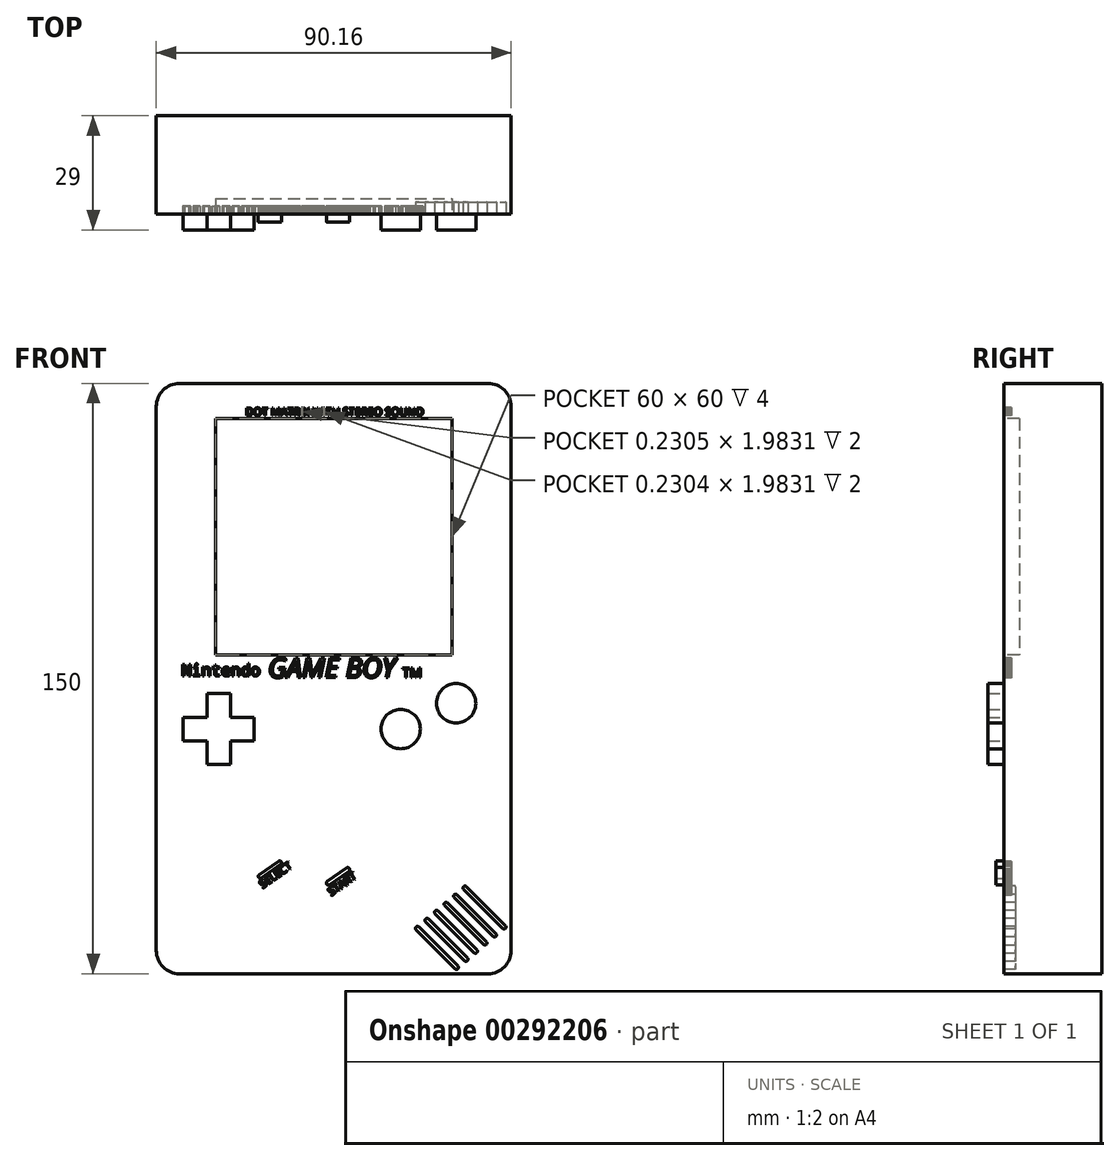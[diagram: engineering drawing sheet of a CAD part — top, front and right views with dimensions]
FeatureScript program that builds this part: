
annotation { "Feature Type Name" : "Feature", "Feature Type Description" : "" }
export const myFeature = defineFeature(function(context is Context, id is Id, definition is map)
    precondition{}
    {
        {
            var Q0;
            Q0=qCreatedBy(makeId("Front.planeOp"),FACE);
            var sketch = newSketch(context, id + "F0", { "sketchPlane" : qUnion([Q0])});
            skLineSegment(sketch, "E0", {"start": v(-45.08, 81.93) * mm, "end": v(-45.08, -35.2) * mm});
            skLineSegment(sketch, "E1", {"start": v(-45.08, -35.2) * mm, "end": v(-45.08, -56.28) * mm});
            skLineSegment(sketch, "E2", {"start": v(-39.18, 87.83) * mm, "end": v(0, 87.83) * mm});
            skLineSegment(sketch, "E3", {"start": v(0, 87.83) * mm, "end": v(0, -62.17) * mm, "construction": true});
            skLineSegment(sketch, "E4", {"start": v(0, -62.17) * mm, "end": v(-39.18, -62.17) * mm});
            skLineSegment(sketch, "E5.MirrorCS", {"start": v(45.08, -35.2) * mm, "end": v(45.08, -56.27) * mm});
            skLineSegment(sketch, "E6.MirrorCS", {"start": v(39.18, 87.83) * mm, "end": v(0, 87.83) * mm});
            skLineSegment(sketch, "E7.MirrorCS", {"start": v(0, -62.17) * mm, "end": v(39.18, -62.17) * mm});
            skLineSegment(sketch, "E8.MirrorCS", {"start": v(45.08, 81.93) * mm, "end": v(45.08, -35.2) * mm});
            skPoint(sketch, "E9.visualSharp", {"position": v(-45.08, 87.83) * mm});
            skArc(sketch, "E9.filletArc", {"start": v(-39.18, 87.83) * mm, "mid": v(-43.35, 86.1) * mm, "end": v(-45.08, 81.93) * mm});
            skPoint(sketch, "E10.visualSharp", {"position": v(-45.08, -62.17) * mm});
            skArc(sketch, "E10.filletArc", {"start": v(-45.08, -56.28) * mm, "mid": v(-43.35, -60.44) * mm, "end": v(-39.18, -62.17) * mm});
            skPoint(sketch, "E11.visualSharp", {"position": v(45.08, 87.83) * mm});
            skArc(sketch, "E11.filletArc", {"start": v(45.08, 81.93) * mm, "mid": v(43.35, 86.1) * mm, "end": v(39.18, 87.83) * mm});
            skPoint(sketch, "E12.visualSharp", {"position": v(45.08, -62.17) * mm});
            skArc(sketch, "E12.filletArc", {"start": v(39.18, -62.17) * mm, "mid": v(43.35, -60.44) * mm, "end": v(45.08, -56.27) * mm});
            skSolve(sketch);
        }
        {
            var Q0;
            Q0=makeQuery(id+"F0.imprint","IMPRINT",FACE,{"disambiguationData":[TD([[makeQuery(id+"F0.imprint","IMPRINT",EDGE,{"derivedFrom":sQuery(id+"F0.wireOp",EDGE,"E0")}),1.0]])]});
            extrude(context, id + "F1", {"entities" : qUnion([Q0]), "depth" : 25 * mm});
        }
        {
            var Q0;
            Q0=makeQuery(id+"F1.opExtrude","CAP_FACE",FACE,{"disambiguationData":[OSD([sQuery(id+"F0.wireOp",EDGE,"E0"),sQuery(id+"F0.wireOp",EDGE,"E1"),sQuery(id+"F0.wireOp",EDGE,"E2"),sQuery(id+"F0.wireOp",EDGE,"E4"),sQuery(id+"F0.wireOp",EDGE,"E5.MirrorCS"),sQuery(id+"F0.wireOp",EDGE,"E6.MirrorCS"),sQuery(id+"F0.wireOp",EDGE,"E7.MirrorCS"),sQuery(id+"F0.wireOp",EDGE,"E8.MirrorCS"),sQuery(id+"F0.wireOp",EDGE,"E9.filletArc"),sQuery(id+"F0.wireOp",EDGE,"E10.filletArc"),sQuery(id+"F0.wireOp",EDGE,"E11.filletArc"),sQuery(id+"F0.wireOp",EDGE,"E12.filletArc")])],"isStart":false});
            var sketch = newSketch(context, id + "F2", { "sketchPlane" : qUnion([Q0])});
            skPoint(sketch, "E13.centerSnap0", {"position": v(45.08, 12.83) * mm});
            skCircle(sketch, "E14", {"center": v(31.09, 6.56) * mm, "radius": 5 * mm});
            skCircle(sketch, "E15", {"center": v(17, 0) * mm, "radius": 5 * mm});
            skLineSegment(sketch, "E16", {"start": v(-29.21, 14.04) * mm, "end": v(-29.21, -22.61) * mm, "construction": true});
            skLineSegment(sketch, "E17", {"start": v(-38.21, 0) * mm, "end": v(-38.21, 3) * mm});
            skLineSegment(sketch, "E18", {"start": v(-38.21, 3) * mm, "end": v(-32.21, 3) * mm});
            skLineSegment(sketch, "E19", {"start": v(-32.21, 3) * mm, "end": v(-32.21, 9) * mm});
            skLineSegment(sketch, "E20", {"start": v(-32.21, 9) * mm, "end": v(-29.21, 9) * mm});
            skLineSegment(sketch, "E21.MirrorCS", {"start": v(-20.21, 0) * mm, "end": v(-20.21, 3) * mm});
            skLineSegment(sketch, "E22.MirrorCS", {"start": v(-20.21, 3) * mm, "end": v(-26.21, 3) * mm});
            skLineSegment(sketch, "E23.MirrorCS", {"start": v(-26.21, 3) * mm, "end": v(-26.21, 9) * mm});
            skLineSegment(sketch, "E24.MirrorCS", {"start": v(-26.21, 9) * mm, "end": v(-29.21, 9) * mm});
            skLineSegment(sketch, "E25", {"start": v(-47.45, 0) * mm, "end": v(-14.16, 0) * mm, "construction": true});
            skLineSegment(sketch, "E26.MirrorCS", {"start": v(-38.21, 0) * mm, "end": v(-38.21, -3) * mm});
            skLineSegment(sketch, "E27.MirrorCS", {"start": v(-38.21, -3) * mm, "end": v(-32.21, -3) * mm});
            skLineSegment(sketch, "E28.MirrorCS", {"start": v(-32.21, -3) * mm, "end": v(-32.21, -9) * mm});
            skLineSegment(sketch, "E29.MirrorCS", {"start": v(-32.21, -9) * mm, "end": v(-29.21, -9) * mm});
            skLineSegment(sketch, "E30.MirrorCS", {"start": v(-26.21, -9) * mm, "end": v(-29.21, -9) * mm});
            skLineSegment(sketch, "E31.MirrorCS", {"start": v(-26.21, -3) * mm, "end": v(-26.21, -9) * mm});
            skLineSegment(sketch, "E32.MirrorCS", {"start": v(-20.21, -3) * mm, "end": v(-26.21, -3) * mm});
            skLineSegment(sketch, "E33.MirrorCS", {"start": v(-20.21, 0) * mm, "end": v(-20.21, -3) * mm});
            skLineSegment(sketch, "E34", {"start": v(0, 79.93) * mm, "end": v(0, 21.08) * mm, "construction": true});
            skLineSegment(sketch, "E35", {"start": v(0, 79.93) * mm, "end": v(-30, 79.93) * mm});
            skLineSegment(sketch, "E36", {"start": v(-30, 79.93) * mm, "end": v(-30, 19.93) * mm});
            skLineSegment(sketch, "E37", {"start": v(-30, 19.93) * mm, "end": v(0, 19.93) * mm});
            skLineSegment(sketch, "E38.MirrorCS", {"start": v(0, 79.93) * mm, "end": v(30, 79.93) * mm});
            skLineSegment(sketch, "E39.MirrorCS", {"start": v(30, 79.93) * mm, "end": v(30, 19.93) * mm});
            skLineSegment(sketch, "E40.MirrorCS", {"start": v(30, 19.93) * mm, "end": v(0, 19.93) * mm});
            skSolve(sketch);
        }
        {
            var Q0;
            Q0=makeQuery(id+"F2.imprint","IMPRINT",FACE,{"disambiguationData":[TD([[makeQuery(id+"F2.imprint","IMPRINT",EDGE,{"derivedFrom":sQuery(id+"F2.wireOp",EDGE,"E14")}),1.0]])]});
            var Q1;
            Q1=makeQuery(id+"F2.imprint","IMPRINT",FACE,{"disambiguationData":[TD([[makeQuery(id+"F2.imprint","IMPRINT",EDGE,{"derivedFrom":sQuery(id+"F2.wireOp",EDGE,"E15")}),1.0]])]});
            var Q2;
            Q2=makeQuery(id+"F2.imprint","IMPRINT",FACE,{"disambiguationData":[TD([[makeQuery(id+"F2.imprint","IMPRINT",EDGE,{"derivedFrom":sQuery(id+"F2.wireOp",EDGE,"E17")}),-1.0]])]});
            extrude(context, id + "F3", {"entities" : qUnion([Q0, Q1, Q2]), "operationType" : NewBodyOperationType.ADD, "depth" : 4 * mm});
        }
        {
            var Q0;
            Q0=makeQuery(id+"F1.opExtrude","CAP_FACE",FACE,{"disambiguationData":[OSD([sQuery(id+"F0.wireOp",EDGE,"E0"),sQuery(id+"F0.wireOp",EDGE,"E1"),sQuery(id+"F0.wireOp",EDGE,"E2"),sQuery(id+"F0.wireOp",EDGE,"E4"),sQuery(id+"F0.wireOp",EDGE,"E5.MirrorCS"),sQuery(id+"F0.wireOp",EDGE,"E6.MirrorCS"),sQuery(id+"F0.wireOp",EDGE,"E7.MirrorCS"),sQuery(id+"F0.wireOp",EDGE,"E8.MirrorCS"),sQuery(id+"F0.wireOp",EDGE,"E9.filletArc"),sQuery(id+"F0.wireOp",EDGE,"E10.filletArc"),sQuery(id+"F0.wireOp",EDGE,"E11.filletArc"),sQuery(id+"F0.wireOp",EDGE,"E12.filletArc")])],"isStart":false});
            var sketch = newSketch(context, id + "F4", { "sketchPlane" : qUnion([Q0])});
            skSolve(sketch);
        }
        {
            var Q0;
            Q0=makeQuery(id+"F4.imprint","IMPRINT",FACE,{"disambiguationData":[TD([[makeQuery(id+"F4.imprint","IMPRINT",EDGE,{"derivedFrom":makeQuery(id+"F1.opExtrude","CAP_EDGE",EDGE,{"disambiguationData":[OSD([sQuery(id+"F0.wireOp",EDGE,"E9.filletArc")])],"isStart":false})}),1.0]])]});
            var sketch = newSketch(context, id + "F5", { "sketchPlane" : qUnion([Q0])});
            skLineSegment(sketch, "E41.bottom", {"start": v(-30, 78.85) * mm, "end": v(30, 78.85) * mm});
            skLineSegment(sketch, "E41.top", {"start": v(-30, 18.85) * mm, "end": v(30, 18.85) * mm});
            skLineSegment(sketch, "E41.left", {"start": v(-30, 78.85) * mm, "end": v(-30, 18.85) * mm});
            skLineSegment(sketch, "E41.right", {"start": v(30, 78.85) * mm, "end": v(30, 18.85) * mm});
            skLineSegment(sketch, "E42", {"start": v(0, 0) * mm, "end": v(0, 81.4) * mm, "construction": true});
            skLineSegment(sketch, "E43", {"start": v(0, 81.4) * mm, "end": v(0, 43.76) * mm, "construction": true});
            skSolve(sketch);
        }
        {
            var Q0;
            Q0 = qSketchRegion(id + "F5", true);
            var Q1;
            Q1=makeQuery(id+"F5.imprint","IMPRINT",FACE,{"disambiguationData":[TD([[makeQuery(id+"F5.imprint","IMPRINT",EDGE,{"derivedFrom":sQuery(id+"F5.wireOp",EDGE,"E41.bottom")}),-1.0]])]});
            extrude(context, id + "F6", {"entities" : qUnion([Q0, Q1]), "operationType" : NewBodyOperationType.REMOVE, "oppositeDirection" : true, "depth" : 4 * mm});
        }
        {
            var Q0;
            Q0=makeQuery(id+"F4.imprint","IMPRINT",FACE,{"disambiguationData":[TD([[makeQuery(id+"F4.imprint","IMPRINT",EDGE,{"derivedFrom":makeQuery(id+"F1.opExtrude","CAP_EDGE",EDGE,{"disambiguationData":[OSD([sQuery(id+"F0.wireOp",EDGE,"E9.filletArc")])],"isStart":false})}),1.0]])]});
            var sketch = newSketch(context, id + "F7", { "sketchPlane" : qUnion([Q0])});
            skLineSegment(sketch, "E44", {"start": v(33.02, -40.75) * mm, "end": v(42.92, -50.65) * mm});
            skLineSegment(sketch, "E45", {"start": v(33.02, -40.04) * mm, "end": v(33.02, -40.04) * mm});
            skLineSegment(sketch, "E46", {"start": v(33.72, -40.04) * mm, "end": v(43.63, -49.94) * mm});
            skLineSegment(sketch, "E47", {"start": v(43.62, -50.65) * mm, "end": v(43.62, -50.65) * mm});
            skPoint(sketch, "E48.visualSharp", {"position": v(32.66, -40.4) * mm});
            skArc(sketch, "E48.filletArc", {"start": v(33.02, -40.04) * mm, "mid": v(32.87, -40.4) * mm, "end": v(33.02, -40.75) * mm});
            skPoint(sketch, "E49.visualSharp", {"position": v(33.37, -39.69) * mm});
            skArc(sketch, "E49.filletArc", {"start": v(33.72, -40.04) * mm, "mid": v(33.37, -39.9) * mm, "end": v(33.02, -40.04) * mm});
            skPoint(sketch, "E50.visualSharp", {"position": v(43.27, -51) * mm});
            skArc(sketch, "E50.filletArc", {"start": v(42.92, -50.65) * mm, "mid": v(43.27, -50.8) * mm, "end": v(43.62, -50.65) * mm});
            skPoint(sketch, "E51.visualSharp", {"position": v(43.98, -50.3) * mm});
            skArc(sketch, "E51.filletArc", {"start": v(43.62, -50.65) * mm, "mid": v(43.77, -50.3) * mm, "end": v(43.63, -49.94) * mm});
            skLineSegment(sketch, "E52", {"start": v(26.9, -56.2) * mm, "end": v(43.42, -39.67) * mm, "construction": true});
            skLineSegment(sketch, "E53.1.0.0", {"start": v(30.6, -42.8) * mm, "end": v(40.5, -52.7) * mm});
            skLineSegment(sketch, "E53.1.0.1", {"start": v(31.3, -42.1) * mm, "end": v(41.2, -52) * mm});
            skArc(sketch, "E53.1.0.2", {"start": v(30.6, -42.1) * mm, "mid": v(30.45, -42.45) * mm, "end": v(30.6, -42.8) * mm});
            skArc(sketch, "E53.1.0.3", {"start": v(31.3, -42.1) * mm, "mid": v(30.95, -41.95) * mm, "end": v(30.6, -42.1) * mm});
            skArc(sketch, "E53.1.0.4", {"start": v(40.5, -52.7) * mm, "mid": v(40.85, -52.85) * mm, "end": v(41.2, -52.7) * mm});
            skArc(sketch, "E53.1.0.5", {"start": v(41.2, -52.7) * mm, "mid": v(41.35, -52.35) * mm, "end": v(41.2, -52) * mm});
            skLineSegment(sketch, "E53.2.0.0", {"start": v(28.18, -44.85) * mm, "end": v(38.08, -54.75) * mm});
            skLineSegment(sketch, "E53.2.0.1", {"start": v(28.89, -44.14) * mm, "end": v(38.79, -54.04) * mm});
            skArc(sketch, "E53.2.0.2", {"start": v(28.18, -44.14) * mm, "mid": v(28.03, -44.5) * mm, "end": v(28.18, -44.85) * mm});
            skArc(sketch, "E53.2.0.3", {"start": v(28.89, -44.14) * mm, "mid": v(28.53, -44) * mm, "end": v(28.18, -44.14) * mm});
            skArc(sketch, "E53.2.0.4", {"start": v(38.08, -54.75) * mm, "mid": v(38.43, -54.9) * mm, "end": v(38.79, -54.75) * mm});
            skArc(sketch, "E53.2.0.5", {"start": v(38.79, -54.75) * mm, "mid": v(38.93, -54.4) * mm, "end": v(38.79, -54.04) * mm});
            skLineSegment(sketch, "E53.3.0.0", {"start": v(25.76, -46.9) * mm, "end": v(35.66, -56.8) * mm});
            skLineSegment(sketch, "E53.3.0.1", {"start": v(26.47, -46.2) * mm, "end": v(36.37, -56.1) * mm});
            skArc(sketch, "E53.3.0.2", {"start": v(25.76, -46.2) * mm, "mid": v(25.62, -46.55) * mm, "end": v(25.76, -46.9) * mm});
            skArc(sketch, "E53.3.0.3", {"start": v(26.47, -46.2) * mm, "mid": v(26.12, -46.05) * mm, "end": v(25.76, -46.2) * mm});
            skArc(sketch, "E53.3.0.4", {"start": v(35.66, -56.8) * mm, "mid": v(36.02, -56.95) * mm, "end": v(36.37, -56.8) * mm});
            skArc(sketch, "E53.3.0.5", {"start": v(36.37, -56.8) * mm, "mid": v(36.52, -56.45) * mm, "end": v(36.37, -56.1) * mm});
            skLineSegment(sketch, "E53.4.0.0", {"start": v(23.34, -48.95) * mm, "end": v(33.24, -58.85) * mm});
            skLineSegment(sketch, "E53.4.0.1", {"start": v(24.05, -48.24) * mm, "end": v(33.95, -58.15) * mm});
            skArc(sketch, "E53.4.0.2", {"start": v(23.34, -48.24) * mm, "mid": v(23.2, -48.6) * mm, "end": v(23.34, -48.95) * mm});
            skArc(sketch, "E53.4.0.3", {"start": v(24.05, -48.24) * mm, "mid": v(23.7, -48.1) * mm, "end": v(23.34, -48.24) * mm});
            skArc(sketch, "E53.4.0.4", {"start": v(33.24, -58.85) * mm, "mid": v(33.6, -59) * mm, "end": v(33.95, -58.85) * mm});
            skArc(sketch, "E53.4.0.5", {"start": v(33.95, -58.85) * mm, "mid": v(34.1, -58.5) * mm, "end": v(33.95, -58.15) * mm});
            skLineSegment(sketch, "E53.5.0.0", {"start": v(20.92, -51) * mm, "end": v(30.83, -60.9) * mm});
            skLineSegment(sketch, "E53.5.0.1", {"start": v(21.63, -50.3) * mm, "end": v(31.53, -60.2) * mm});
            skArc(sketch, "E53.5.0.2", {"start": v(20.92, -50.3) * mm, "mid": v(20.78, -50.65) * mm, "end": v(20.92, -51) * mm});
            skArc(sketch, "E53.5.0.3", {"start": v(21.63, -50.3) * mm, "mid": v(21.28, -50.15) * mm, "end": v(20.92, -50.3) * mm});
            skArc(sketch, "E53.5.0.4", {"start": v(30.83, -60.9) * mm, "mid": v(31.18, -61.05) * mm, "end": v(31.53, -60.9) * mm});
            skArc(sketch, "E53.5.0.5", {"start": v(31.53, -60.9) * mm, "mid": v(31.68, -60.55) * mm, "end": v(31.53, -60.2) * mm});
            skLineSegment(sketch, "E53.direction1", {"start": v(42.92, -50.65) * mm, "end": v(40.5, -52.7) * mm, "construction": true});
            skSolve(sketch);
        }
        {
            var Q0;
            Q0 = qSketchRegion(id + "F7", true);
            extrude(context, id + "F8", {"entities" : qUnion([Q0]), "operationType" : NewBodyOperationType.REMOVE, "oppositeDirection" : true, "depth" : 3 * mm});
        }
        {
            var Q0;
            Q0=makeQuery(id+"F4.imprint","IMPRINT",FACE,{"disambiguationData":[TD([[makeQuery(id+"F4.imprint","IMPRINT",EDGE,{"derivedFrom":makeQuery(id+"F1.opExtrude","CAP_EDGE",EDGE,{"disambiguationData":[OSD([sQuery(id+"F0.wireOp",EDGE,"E9.filletArc")])],"isStart":false})}),1.0]])]});
            var sketch = newSketch(context, id + "F9", { "sketchPlane" : qUnion([Q0])});
            skLineSegment(sketch, "E54", {"start": v(-14.03, -33.56) * mm, "end": v(-18.95, -37) * mm});
            skLineSegment(sketch, "E55", {"start": v(-19.07, -37.7) * mm, "end": v(-19.07, -37.7) * mm});
            skLineSegment(sketch, "E56", {"start": v(-18.38, -37.83) * mm, "end": v(-13.46, -34.38) * mm});
            skLineSegment(sketch, "E57", {"start": v(-13.33, -33.7) * mm, "end": v(-13.33, -33.7) * mm});
            skPoint(sketch, "E58.visualSharp", {"position": v(-18.79, -38.11) * mm});
            skArc(sketch, "E58.filletArc", {"start": v(-19.07, -37.7) * mm, "mid": v(-18.75, -37.9) * mm, "end": v(-18.38, -37.83) * mm});
            skPoint(sketch, "E59.visualSharp", {"position": v(-19.36, -37.3) * mm});
            skArc(sketch, "E59.filletArc", {"start": v(-18.95, -37) * mm, "mid": v(-19.16, -37.33) * mm, "end": v(-19.07, -37.7) * mm});
            skPoint(sketch, "E60.visualSharp", {"position": v(-13.06, -34.1) * mm});
            skArc(sketch, "E60.filletArc", {"start": v(-13.46, -34.38) * mm, "mid": v(-13.25, -34.07) * mm, "end": v(-13.33, -33.7) * mm});
            skPoint(sketch, "E61.visualSharp", {"position": v(-13.6, -33.27) * mm});
            skArc(sketch, "E61.filletArc", {"start": v(-13.33, -33.7) * mm, "mid": v(-13.65, -33.48) * mm, "end": v(-14.03, -33.56) * mm});
            skPoint(sketch, "E62.1.0.0", {"position": v(4.22, -35.83) * mm});
            skLineSegment(sketch, "E62.1.0.1", {"start": v(3.25, -35.28) * mm, "end": v(-1.66, -38.73) * mm});
            skPoint(sketch, "E62.1.0.2", {"position": v(-1.5, -39.83) * mm});
            skPoint(sketch, "E62.1.0.3", {"position": v(-2.07, -39.01) * mm});
            skLineSegment(sketch, "E62.1.0.4", {"start": v(-1.1, -39.55) * mm, "end": v(3.83, -36.1) * mm});
            skPoint(sketch, "E62.1.0.5", {"position": v(3.68, -34.99) * mm});
            skArc(sketch, "E62.1.0.6", {"start": v(3.83, -36.1) * mm, "mid": v(4.03, -35.79) * mm, "end": v(3.96, -35.42) * mm});
            skArc(sketch, "E62.1.0.7", {"start": v(-1.66, -38.73) * mm, "mid": v(-1.87, -39.05) * mm, "end": v(-1.79, -39.42) * mm});
            skArc(sketch, "E62.1.0.8", {"start": v(3.96, -35.42) * mm, "mid": v(3.64, -35.2) * mm, "end": v(3.25, -35.28) * mm});
            skArc(sketch, "E62.1.0.9", {"start": v(-1.79, -39.42) * mm, "mid": v(-1.46, -39.63) * mm, "end": v(-1.1, -39.55) * mm});
            skLineSegment(sketch, "E62.direction1", {"start": v(-18.79, -38.11) * mm, "end": v(-1.5, -39.83) * mm, "construction": true});
            skSolve(sketch);
        }
        {
            var Q0;
            Q0=makeQuery(id+"F4.imprint","IMPRINT",FACE,{"disambiguationData":[TD([[makeQuery(id+"F4.imprint","IMPRINT",EDGE,{"derivedFrom":makeQuery(id+"F1.opExtrude","CAP_EDGE",EDGE,{"disambiguationData":[OSD([sQuery(id+"F0.wireOp",EDGE,"E9.filletArc")])],"isStart":false})}),1.0]])]});
            var sketch = newSketch(context, id + "F10", { "sketchPlane" : qUnion([Q0])});
            skText(sketch, "E63", { "text": "Nintendo", "fontName": "DroidSansMono.ttf"});
            skText(sketch, "E64", { "text": "GAME BOY", "fontName": "OpenSans-Italic.ttf"});
            skText(sketch, "E65", { "text": "TM", "fontName": "OpenSans-Regular.ttf"});
            const initialGuessF10  = {"E63": [-0.03863, 0.01349, 1, 0, 0.003], "E64": [-0.01667, 0.01307, 1, 0, 0.005], "E65": [0.01747, 0.01314, 1, 0, 0.00242]};
            skSetInitialGuess(sketch, initialGuessF10);
            skSolve(sketch);
        }
        {
            var Q0;
            Q0 = qSketchRegion(id + "F10", true);
            extrude(context, id + "F11", {"entities" : qUnion([Q0]), "operationType" : NewBodyOperationType.REMOVE, "oppositeDirection" : true, "depth" : 2 * mm});
        }
        {
            var Q0;
            Q0 = qSketchRegion(id + "F9", true);
            extrude(context, id + "F12", {"entities" : qUnion([Q0]), "operationType" : NewBodyOperationType.ADD, "depth" : 2 * mm});
        }
        {
            var Q0;
            Q0=makeQuery(id+"F4.imprint","IMPRINT",FACE,{"disambiguationData":[TD([[makeQuery(id+"F4.imprint","IMPRINT",EDGE,{"derivedFrom":makeQuery(id+"F1.opExtrude","CAP_EDGE",EDGE,{"disambiguationData":[OSD([sQuery(id+"F0.wireOp",EDGE,"E9.filletArc")])],"isStart":false})}),1.0]])]});
            var sketch = newSketch(context, id + "F13", { "sketchPlane" : qUnion([Q0])});
            skText(sketch, "E66", { "text": "DOT MATRIX WITH STEREO SOUND", "fontName": "OpenSans-Regular.ttf"});
            const initialGuessF13  = {"E66": [-0.02244, 0.07963, 1, 0, 0.002]};
            skSetInitialGuess(sketch, initialGuessF13);
            skSolve(sketch);
        }
        {
            var Q0;
            Q0 = qSketchRegion(id + "F13", true);
            extrude(context, id + "F14", {"entities" : qUnion([Q0]), "operationType" : NewBodyOperationType.REMOVE, "oppositeDirection" : true, "depth" : 2 * mm});
        }
        {
            var Q0;
            Q0 = qSketchRegion(id + "F10", true);
            extrude(context, id + "F15", {"entities" : qUnion([Q0]), "operationType" : NewBodyOperationType.REMOVE, "oppositeDirection" : true, "depth" : 2 * mm});
        }
        {
            var Q0;
            Q0=makeQuery(id+"F4.imprint","IMPRINT",FACE,{"disambiguationData":[TD([[makeQuery(id+"F4.imprint","IMPRINT",EDGE,{"derivedFrom":makeQuery(id+"F1.opExtrude","CAP_EDGE",EDGE,{"disambiguationData":[OSD([sQuery(id+"F0.wireOp",EDGE,"E9.filletArc")])],"isStart":false})}),1.0]])]});
            var sketch = newSketch(context, id + "F16", { "sketchPlane" : qUnion([Q0])});
            skText(sketch, "E67", { "text": "SELECT", "fontName": "OpenSans-Regular.ttf"});
            skText(sketch, "E68", { "text": "START", "fontName": "OpenSans-Regular.ttf"});
            const initialGuessF16  = {"E67": [-0.01807, -0.04053, 0.81915, 0.57358, 0.002], "E68": [-0.00062, -0.04243, 0.81915, 0.57358, 0.002]};
            skSetInitialGuess(sketch, initialGuessF16);
            skSolve(sketch);
        }
        {
            var Q0;
            Q0 = qSketchRegion(id + "F16", true);
            extrude(context, id + "F17", {"entities" : qUnion([Q0]), "operationType" : NewBodyOperationType.REMOVE, "oppositeDirection" : true, "depth" : 2 * mm});
        }
    });
